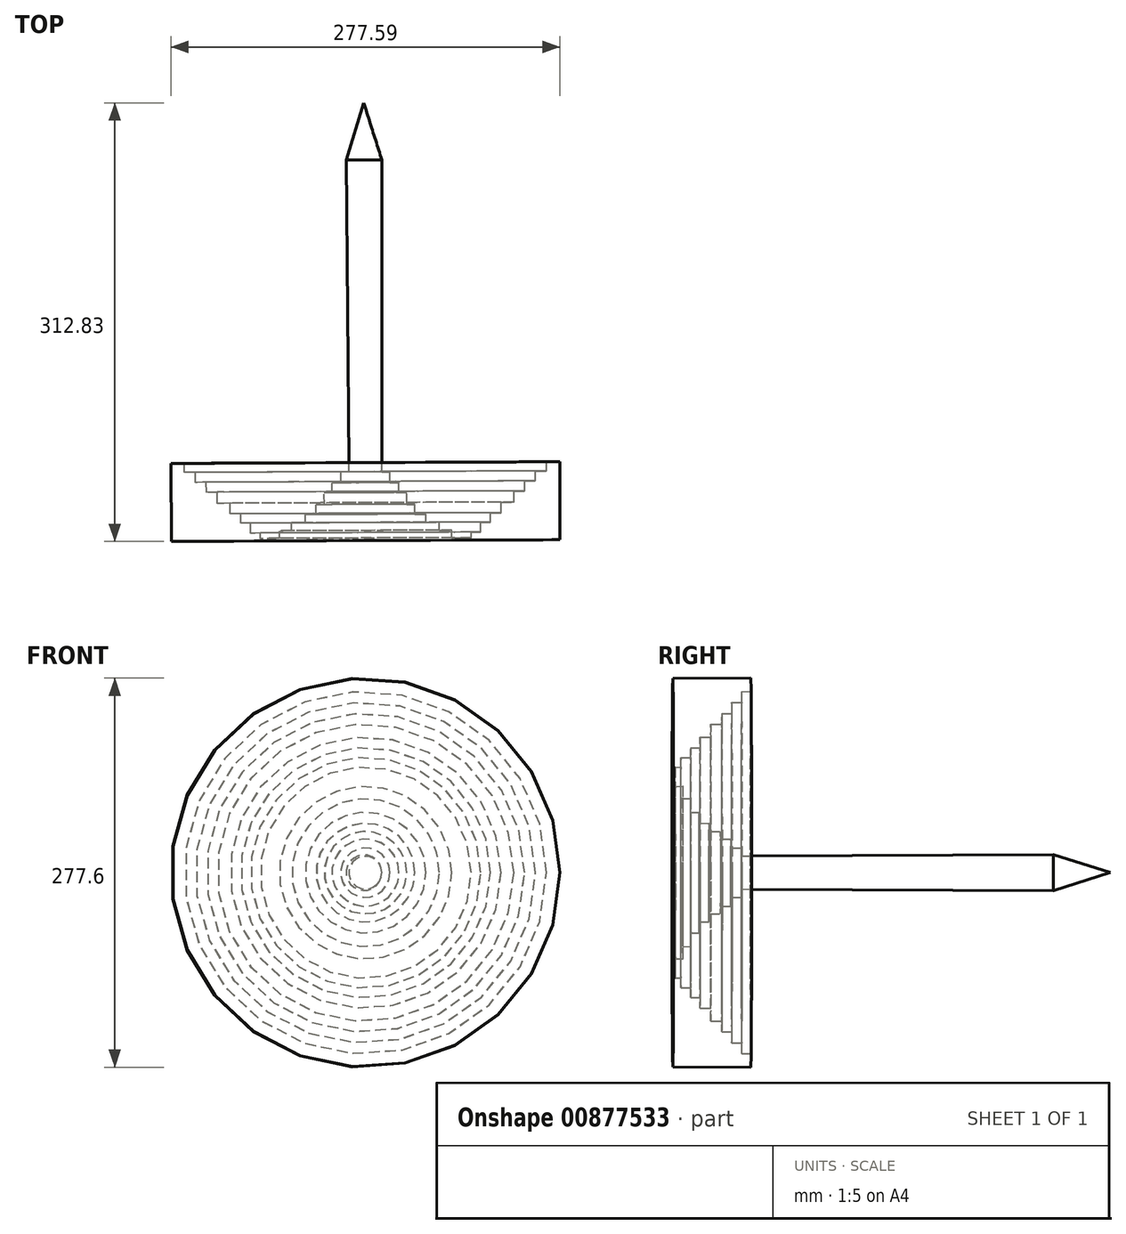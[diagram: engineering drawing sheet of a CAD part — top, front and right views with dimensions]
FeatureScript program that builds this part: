
annotation { "Feature Type Name" : "Feature", "Feature Type Description" : "" }
export const myFeature = defineFeature(function(context is Context, id is Id, definition is map)
    precondition{}
    {
        {
            var Q0;
            Q0=qCreatedBy(makeId("Top.planeOp"),FACE);
            var sketch = newSketch(context, id + "F0", { "sketchPlane" : qUnion([Q0])});
            skLineSegment(sketch, "E0", {"start": v(71.94, 0) * mm, "end": v(71.94, 55.62) * mm});
            skLineSegment(sketch, "E1", {"start": v(71.94, 55.62) * mm, "end": v(62.36, 55.62) * mm});
            skLineSegment(sketch, "E2", {"start": v(62.36, 55.62) * mm, "end": v(62.36, 49.05) * mm});
            skLineSegment(sketch, "E3", {"start": v(62.36, 49.05) * mm, "end": v(54.55, 49.05) * mm});
            skLineSegment(sketch, "E4", {"start": v(54.55, 49.05) * mm, "end": v(54.55, 41.96) * mm});
            skLineSegment(sketch, "E5", {"start": v(54.55, 41.96) * mm, "end": v(46.75, 41.96) * mm});
            skLineSegment(sketch, "E6", {"start": v(46.75, 41.96) * mm, "end": v(46.75, 34.86) * mm});
            skLineSegment(sketch, "E7", {"start": v(46.75, 34.86) * mm, "end": v(39.12, 34.86) * mm});
            skLineSegment(sketch, "E8", {"start": v(39.12, 34.86) * mm, "end": v(39.12, 26.88) * mm});
            skLineSegment(sketch, "E9", {"start": v(39.12, 26.88) * mm, "end": v(29.9, 26.88) * mm});
            skLineSegment(sketch, "E10", {"start": v(29.9, 26.88) * mm, "end": v(29.9, 19.25) * mm});
            skLineSegment(sketch, "E11", {"start": v(29.9, 19.25) * mm, "end": v(22.44, 19.25) * mm});
            skLineSegment(sketch, "E12", {"start": v(22.44, 19.25) * mm, "end": v(22.44, 12.5) * mm});
            skLineSegment(sketch, "E13", {"start": v(22.44, 12.5) * mm, "end": v(15.52, 12.5) * mm});
            skLineSegment(sketch, "E14", {"start": v(15.52, 12.5) * mm, "end": v(15.52, 5.41) * mm});
            skLineSegment(sketch, "E15", {"start": v(15.52, 5.41) * mm, "end": v(8.6, 5.41) * mm});
            skLineSegment(sketch, "E16", {"start": v(8.6, 5.41) * mm, "end": v(8.6, 1.5) * mm});
            skLineSegment(sketch, "E17", {"start": v(8.6, 1.5) * mm, "end": v(-5.06, 1.5) * mm});
            skLineSegment(sketch, "E18", {"start": v(-5.06, 1.5) * mm, "end": v(-5.06, 6.83) * mm});
            skLineSegment(sketch, "E19", {"start": v(-5.06, 6.83) * mm, "end": v(-13.93, 6.83) * mm});
            skLineSegment(sketch, "E20", {"start": v(-13.93, 6.83) * mm, "end": v(-13.93, 12.5) * mm});
            skLineSegment(sketch, "E21", {"start": v(-13.93, 12.5) * mm, "end": v(-23.68, 12.5) * mm});
            skLineSegment(sketch, "E22", {"start": v(-23.68, 12.5) * mm, "end": v(-23.68, 18.18) * mm});
            skLineSegment(sketch, "E23", {"start": v(-23.68, 18.18) * mm, "end": v(-31.49, 18.18) * mm});
            skLineSegment(sketch, "E24", {"start": v(-31.49, 18.18) * mm, "end": v(-31.49, 25.28) * mm});
            skLineSegment(sketch, "E25", {"start": v(-31.49, 25.28) * mm, "end": v(-37.34, 25.28) * mm});
            skLineSegment(sketch, "E26", {"start": v(-37.34, 25.28) * mm, "end": v(-37.34, 33.62) * mm});
            skLineSegment(sketch, "E27", {"start": v(-37.34, 33.62) * mm, "end": v(-42.84, 33.62) * mm});
            skLineSegment(sketch, "E28", {"start": v(-42.84, 33.62) * mm, "end": v(-42.84, 40.71) * mm});
            skLineSegment(sketch, "E29", {"start": v(-42.84, 40.71) * mm, "end": v(-49.23, 40.71) * mm});
            skLineSegment(sketch, "E30", {"start": v(-49.23, 40.71) * mm, "end": v(-49.23, 48.52) * mm});
            skLineSegment(sketch, "E31", {"start": v(-49.23, 48.52) * mm, "end": v(-55.08, 48.52) * mm});
            skLineSegment(sketch, "E32", {"start": v(-66.62, 0) * mm, "end": v(71.94, 0) * mm});
            skLineSegment(sketch, "E33", {"start": v(-66.62, 0) * mm, "end": v(-67.98, 311.6) * mm});
            skLineSegment(sketch, "E34", {"start": v(-55.08, 170.84) * mm, "end": v(-55.08, 48.52) * mm});
            skLineSegment(sketch, "E35", {"start": v(-67.98, 311.6) * mm, "end": v(-55.08, 270.97) * mm});
            skLineSegment(sketch, "E36", {"start": v(-55.08, 270.97) * mm, "end": v(-55.08, 170.84) * mm});
            skSolve(sketch);
        }
        {
            var Q0;
            Q0=makeQuery(id+"F0.imprint","IMPRINT",FACE,{"disambiguationData":[TD([[makeQuery(id+"F0.imprint","IMPRINT",EDGE,{"derivedFrom":sQuery(id+"F0.wireOp",EDGE,"E0")}),1.0]])]});
            var Q1;
            Q1=sQuery(id+"F0.wireOp",EDGE,"E33");
            revolve(context, id + "F1", {"surfaceOperationType" : NewSurfaceOperationType.NEW, "entities" : qUnion([Q0]), "axis" : qUnion([Q1]), "revolveType" : RevolveType.FULL});
        }
    });
